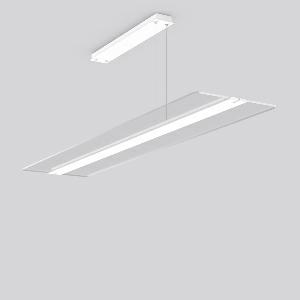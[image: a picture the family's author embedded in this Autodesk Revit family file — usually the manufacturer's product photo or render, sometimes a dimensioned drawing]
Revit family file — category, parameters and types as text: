
# Revit family: twindot_s_312265_002_1_fde0
name_source: partatom
category: Lighting Fixtures
units: mm (PartAtom-declared; Revit-internal decimal feet)

## family parameters
Cut with Voids When Loaded = No
Host = Face
Light Source = No
Part Type = Normal
Room Calculation Point = No
Round Connector Dimension = Use Diameter
Shared = No

## types (1)
- TWINDOT S (1 x LED Modul 840, 8100 lm, 4000)
    Apparent Load = 62 VA
    CIE Flux Codes = 47 77 94 55 100
    Color Rendering = 80
    Color Temperature = 4000
    Default Elevation = 1800 mm
    Description = Series: TWINDOT S
LED pendant luminaire with extremely flat and frameless appearance. Middle bar made of aluminium extrusion profile, powder-coated. Transparent light guide made of UV-resistant acrylic glass (PMMA) with TWINDOT prismatic. Light control with perfectly glare-free TWINDOT technology for pleasantly gentle light with soft shadows. Even and wide indirect and direct light distribution. Direct 55%, indirect 45% light emission. 4-point steel cable suspension, steplessly adjustable. Converter integrated in the canopy (powder-coated white). Power supply through suspension cable. 
Colour: traffic white, matt (RAL 9016)
Length: 1500 mm
Width: 350 mm
Height: 20 mm
Suspension length: 500-1200 mm
Lamp: LED
Socket: without socket
Colour temperature: 4000K
Colour rendering index (CRI): 80
System power: 62 W
Rated luminous flux: 8100 lm
Luminous efficiency: 131 lm/W
Control gear: Regulated power supply
Protection class: I
Type of protection: IP 20
    Height = 20 mm  [stored 0.0656168 ft]
    Lamp = 1 x LED Modul 840
    Lamp Light Flux = 8100 lm
    Lamp count = 1
    Length = 1500 mm
    Lifetime = 50000 h
    Luminous efficacy = 131 lm/W
    Manufacturer = RZB
    ModVariant = No
    Model = 312265.002.1
    Mounting Place = Ceiling
    Mounting Type = Pendant
    Number of Poles = 1
    OnlyDefault = Yes
    Power Factor = 1
    Product Name = TWINDOT S
    Product group = Pendant modular luminaires
    ProductGroupID = 906
    Protection Class = Protection class I
    Protection Degree = IP 20
    RLX_Detail_Level = 1
    RLX_Emergency_Light_Flux = 0 lm
    RLX_Emergency_Type = 0
    RLX_Emergency_Type_DB = No
    RlxData = <blob elided: 36685 chars, md5=ddd95375>
    Socket = socket
    Standby Power = 0 W
    System Light Flux = 8100 lm
    System Power = 62 W
    Type Comments = Product without accessories
    Type Image = 312265.002.jpg
    URL = http://relux.com
    VarID = ---
    Voltage = 230 V
    Voltage Range = 220-240 V
    Weight = 0.00 kg
    Width = 350 mm

note: [stored X ft] marks values corroborated as IEEE doubles in the binary element streams (Revit-internal decimal feet)

## geometry (parser evidence)
native form markers: Blend x4, Sweep x10
no freeform markers — native parametric forms only
